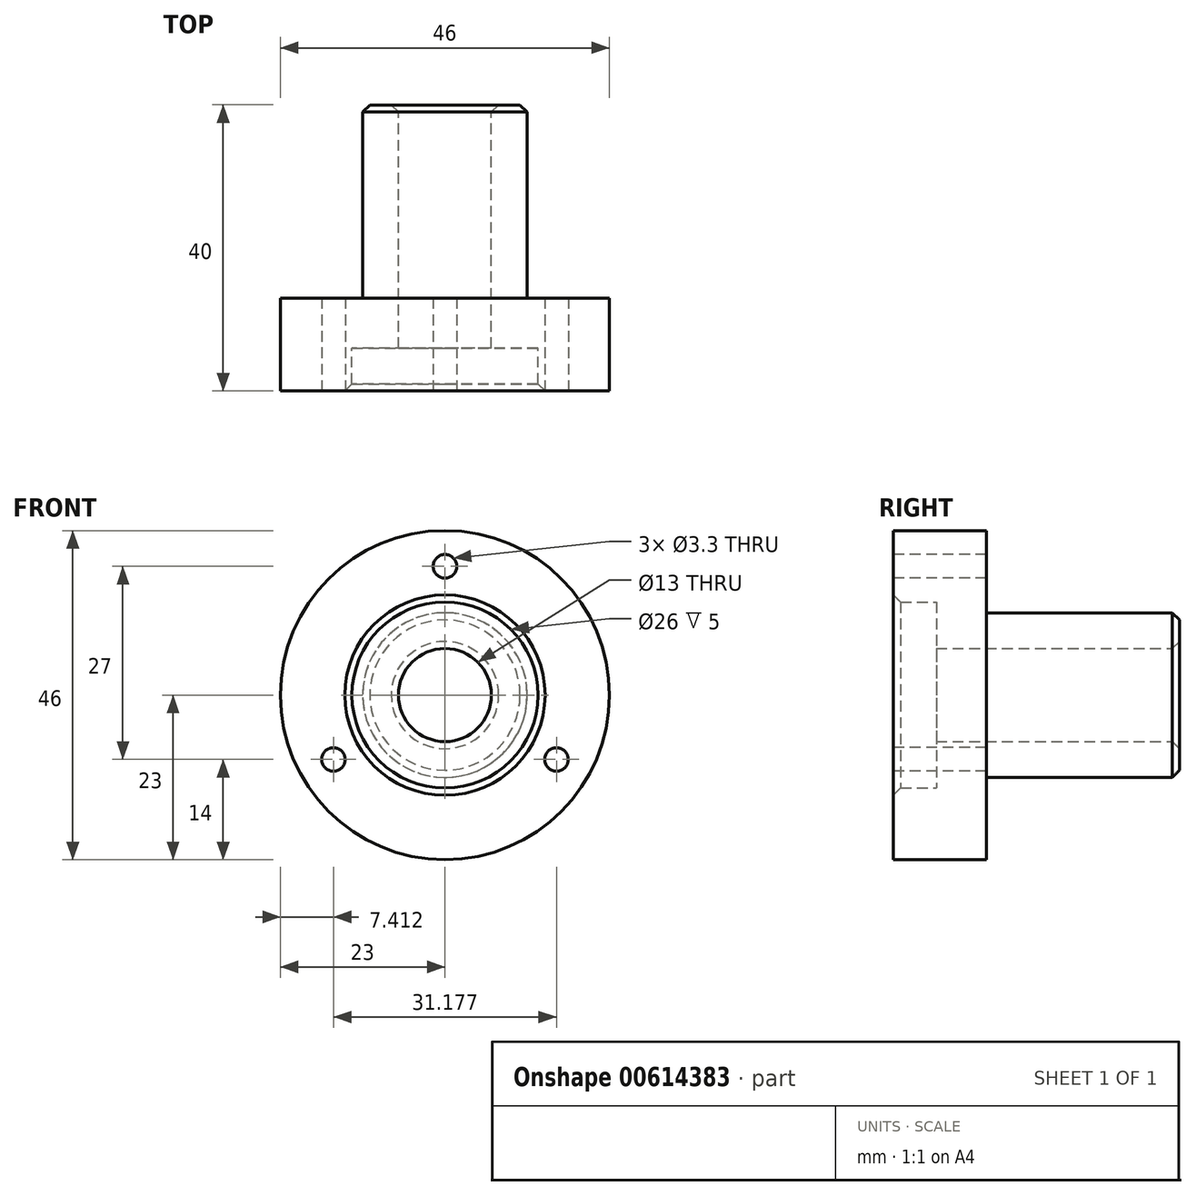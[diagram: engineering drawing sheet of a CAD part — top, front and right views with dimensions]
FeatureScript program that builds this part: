
annotation { "Feature Type Name" : "Feature", "Feature Type Description" : "" }
export const myFeature = defineFeature(function(context is Context, id is Id, definition is map)
    precondition{}
    {
        {
            var Q0;
            Q0=qCreatedBy(makeId("Right.planeOp"),FACE);
            var sketch = newSketch(context, id + "F0", { "sketchPlane" : qUnion([Q0])});
            skLineSegment(sketch, "E0", {"start": v(25.2, 0) * mm, "end": v(-29.58, 0) * mm});
            skLineSegment(sketch, "E1", {"start": v(18.09, 6.5) * mm, "end": v(-15.91, 6.5) * mm});
            skLineSegment(sketch, "E2", {"start": v(-15.91, 6.5) * mm, "end": v(-15.91, 13) * mm});
            skLineSegment(sketch, "E3", {"start": v(-15.91, 13) * mm, "end": v(-21.91, 13) * mm});
            skLineSegment(sketch, "E4", {"start": v(-21.91, 13) * mm, "end": v(-21.91, 23) * mm});
            skLineSegment(sketch, "E5", {"start": v(-21.91, 23) * mm, "end": v(-8.91, 23) * mm});
            skLineSegment(sketch, "E6", {"start": v(-8.91, 23) * mm, "end": v(-8.91, 11.5) * mm});
            skLineSegment(sketch, "E7", {"start": v(-8.91, 11.5) * mm, "end": v(18.09, 11.5) * mm});
            skLineSegment(sketch, "E8", {"start": v(18.09, 11.5) * mm, "end": v(18.09, 6.5) * mm});
            skSolve(sketch);
        }
        {
            var Q0;
            Q0=makeQuery(id+"F0.imprint","IMPRINT",FACE,{"disambiguationData":[TD([[makeQuery(id+"F0.imprint","IMPRINT",EDGE,{"derivedFrom":sQuery(id+"F0.wireOp",EDGE,"E1")}),-1.0]])]});
            var Q1;
            Q1=sQuery(id+"F0.wireOp",EDGE,"E0");
            revolve(context, id + "F1", {"surfaceOperationType" : NewSurfaceOperationType.NEW, "entities" : qUnion([Q0]), "axis" : qUnion([Q1]), "revolveType" : RevolveType.FULL});
        }
        {
            var Q0;
            Q0=makeQuery(id+"F1.opRevolve","SWEPT_EDGE",EDGE,{"disambiguationData":[OSD([sQuery(id+"F0.wireOp",EDGE,"E7"),sQuery(id+"F0.wireOp",EDGE,"E8")])]});
            var Q1;
            Q1=makeQuery(id+"F1.opRevolve","SWEPT_FACE",FACE,{"disambiguationData":[OSD([sQuery(id+"F0.wireOp",EDGE,"E8")])]});
            var Q2;
            Q2=makeQuery(id+"F1.opRevolve","SWEPT_EDGE",EDGE,{"disambiguationData":[OSD([sQuery(id+"F0.wireOp",EDGE,"E3"),sQuery(id+"F0.wireOp",EDGE,"E4")])]});
            chamfer(context, id + "F2", {"entities" : qUnion([Q0, Q1, Q2]), "width" : 1 * mm, "tangentPropagation" : true});
        }
        {
            var Q0;
            Q0=makeQuery(id+"F1.opRevolve","SWEPT_FACE",FACE,{"disambiguationData":[OSD([sQuery(id+"F0.wireOp",EDGE,"E4")])]});
            var sketch = newSketch(context, id + "F3", { "sketchPlane" : qUnion([Q0])});
            skCircle(sketch, "E9.0", {"center": v(0, 0) * mm, "radius": 13 * mm});
            skCircle(sketch, "E10.0", {"center": v(0, 0) * mm, "radius": 23 * mm});
            skLineSegment(sketch, "E11", {"start": v(0, 13) * mm, "end": v(0, 23) * mm, "construction": true});
            skPoint(sketch, "E12", {"position": v(0, 18) * mm});
            skPoint(sketch, "E13.1.0", {"position": v(-15.59, -9) * mm});
            skPoint(sketch, "E13.2.0", {"position": v(15.59, -9) * mm});
            skSolve(sketch);
        }
        {
            var Q0;
            Q0=sQuery(id+"F3.wireOp",VERTEX,"E12");
            var Q1;
            Q1=sQuery(id+"F3.wireOp",VERTEX,"E13.1.0");
            var Q2;
            Q2=sQuery(id+"F3.wireOp",VERTEX,"E13.2.0");
            var Q3;
            Q3=makeQuery(id+"F1.opRevolve","SWEPT_BODY",BODY,{"disambiguationData":[OSD([sQuery(id+"F0.wireOp",EDGE,"E1"),sQuery(id+"F0.wireOp",EDGE,"E2"),sQuery(id+"F0.wireOp",EDGE,"E3"),sQuery(id+"F0.wireOp",EDGE,"E4"),sQuery(id+"F0.wireOp",EDGE,"E5"),sQuery(id+"F0.wireOp",EDGE,"E6"),sQuery(id+"F0.wireOp",EDGE,"E7"),sQuery(id+"F0.wireOp",EDGE,"E8")])]});
            hole(context, id + "F4", {"style" : HoleStyle.SIMPLE, "endStyle" : HoleEndStyle.THROUGH, "standardTappedOrClearance" : lookupTablePath({ "standard" : "ISO", "engagement" : "75%", "pitch" : "0.7 mm", "size" : "M4", "type" : "Tapped" }), "standardBlindInLast" : lookupTablePath({ "standard" : "ISO", "engagement" : "75%", "pitch" : "0.7 mm", "size" : "M4", "type" : "Tapped" }), "holeDiameter" : 3.3 * mm, "majorDiameter" : 4 * mm, "showTappedDepth" : true, "tappedDepth" : 8 * mm, "tapClearance" : 3, "locations" : qUnion([Q0, Q1, Q2]), "scope" : qUnion([Q3])});
        }
    });
